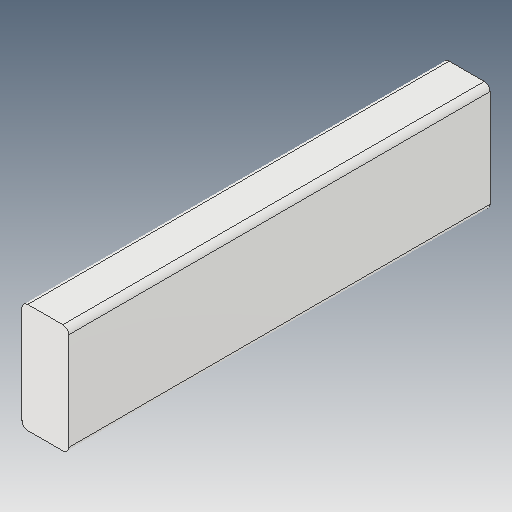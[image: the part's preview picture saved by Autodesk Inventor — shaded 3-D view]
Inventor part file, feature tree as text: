
AUTODESK INVENTOR PART (.ipt)
format: ipt  version: 2023.5 (Build 275446000, 446)  size: 89,600 bytes
history: native  units: in
note: dims shown in document units (in); Inventor stores cm internally (conversion verified against a paired STEP export)
features: fillet x1
ambient origin geometry x8: Origin, YZ Plane, XZ Plane, XY Plane, X Axis, Y Axis, Z Axis, Center Point
bodies: Solid1 (feature_tree)
feature tree (1):
  fillet  "Fillet1"  [1 undecoded]
note: 1 required parameter value undecoded (feature->parameter linkage not recoverable at this tier; creation-order binding heuristic only, values carry confidence <= 0.55)
